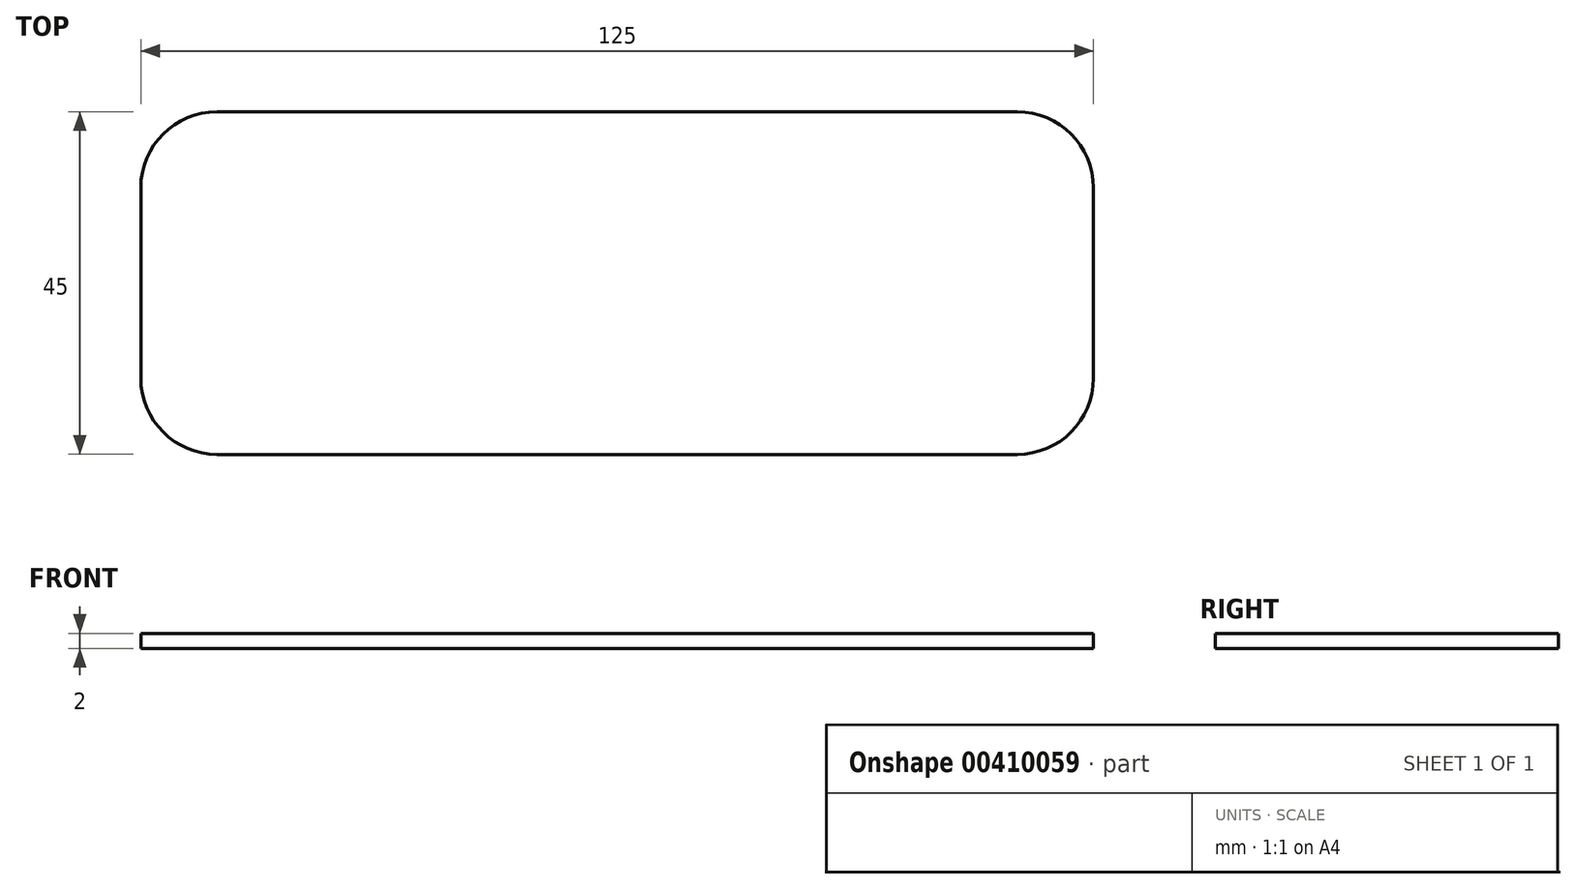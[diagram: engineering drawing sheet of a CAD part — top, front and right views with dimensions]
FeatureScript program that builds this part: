
annotation { "Feature Type Name" : "Feature", "Feature Type Description" : "" }
export const myFeature = defineFeature(function(context is Context, id is Id, definition is map)
    precondition{}
    {
        {
            var Q0;
            Q0=qCreatedBy(makeId("Top.planeOp"),FACE);
            var sketch = newSketch(context, id + "F0", { "sketchPlane" : qUnion([Q0])});
            skLineSegment(sketch, "E0.bottom", {"start": v(-76.61, 28.76) * mm, "end": v(48.39, 28.76) * mm});
            skLineSegment(sketch, "E0.top", {"start": v(-76.61, -16.24) * mm, "end": v(48.39, -16.24) * mm});
            skLineSegment(sketch, "E0.left", {"start": v(-76.61, 28.76) * mm, "end": v(-76.61, -16.24) * mm});
            skLineSegment(sketch, "E0.right", {"start": v(48.39, 28.76) * mm, "end": v(48.39, -16.24) * mm});
            skSolve(sketch);
        }
        {
            var Q0;
            Q0 = qSketchRegion(id + "F0", true);
            extrude(context, id + "F1", {"entities" : qUnion([Q0]), "depth" : 2 * mm, "offsetDistance" : 25 * mm});
        }
        {
            var Q0;
            Q0=makeQuery(id+"F1.opExtrude","SWEPT_EDGE",EDGE,{"disambiguationData":[OSD([sQuery(id+"F0.wireOp",EDGE,"E0.bottom"),sQuery(id+"F0.wireOp",EDGE,"E0.left")])]});
            var Q1;
            Q1=makeQuery(id+"F1.opExtrude","SWEPT_EDGE",EDGE,{"disambiguationData":[OSD([sQuery(id+"F0.wireOp",EDGE,"E0.bottom"),sQuery(id+"F0.wireOp",EDGE,"E0.right")])]});
            var Q2;
            Q2=makeQuery(id+"F1.opExtrude","SWEPT_EDGE",EDGE,{"disambiguationData":[OSD([sQuery(id+"F0.wireOp",EDGE,"E0.top"),sQuery(id+"F0.wireOp",EDGE,"E0.right")])]});
            var Q3;
            Q3=makeQuery(id+"F1.opExtrude","SWEPT_EDGE",EDGE,{"disambiguationData":[OSD([sQuery(id+"F0.wireOp",EDGE,"E0.top"),sQuery(id+"F0.wireOp",EDGE,"E0.left")])]});
            fillet(context, id + "F2", {"entities" : qUnion([Q0, Q1, Q2, Q3]), "radius" : 10 * mm, "tangentPropagation" : true, "allowEdgeOverflow" : false});
        }
    });
